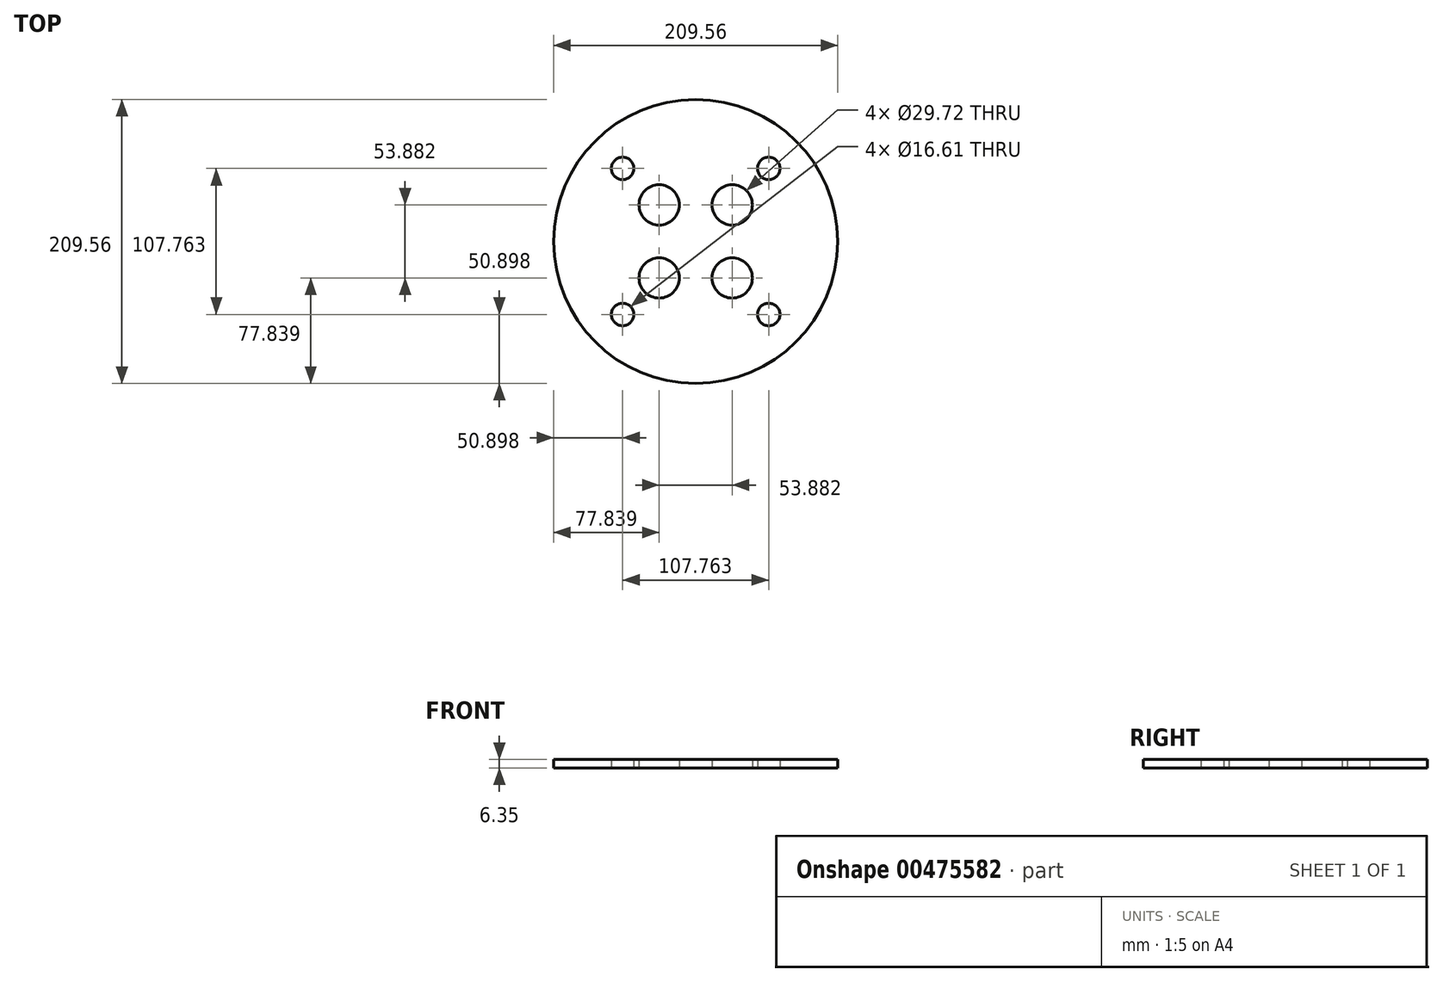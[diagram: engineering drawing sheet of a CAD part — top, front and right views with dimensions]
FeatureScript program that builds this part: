
annotation { "Feature Type Name" : "Feature", "Feature Type Description" : "" }
export const myFeature = defineFeature(function(context is Context, id is Id, definition is map)
    precondition{}
    {
        {
            var Q0;
            Q0=qCreatedBy(makeId("Top.planeOp"),FACE);
            var sketch = newSketch(context, id + "F0", { "sketchPlane" : qUnion([Q0])});
            skCircle(sketch, "E0", {"center": v(0, 0) * mm, "radius": 104.78 * mm});
            skLineSegment(sketch, "E1", {"start": v(0, 0) * mm, "end": v(53.88, 53.88) * mm});
            skLineSegment(sketch, "E2", {"start": v(0, 0) * mm, "end": v(53.88, -53.88) * mm});
            skLineSegment(sketch, "E3", {"start": v(0, 0) * mm, "end": v(-53.88, -53.88) * mm});
            skPoint(sketch, "E4", {"position": v(-26.94, 26.94) * mm});
            skPoint(sketch, "E5", {"position": v(26.94, 26.94) * mm});
            skPoint(sketch, "E6", {"position": v(26.94, -26.94) * mm});
            skPoint(sketch, "E7", {"position": v(-26.94, -26.94) * mm});
            skLineSegment(sketch, "E8", {"start": v(0, 0) * mm, "end": v(-53.88, 53.88) * mm});
            skPoint(sketch, "E9", {"position": v(-53.88, 53.88) * mm});
            skPoint(sketch, "E10", {"position": v(-53.88, -53.88) * mm});
            skPoint(sketch, "E11", {"position": v(53.88, 53.88) * mm});
            skPoint(sketch, "E12", {"position": v(53.88, -53.88) * mm});
            skSolve(sketch);
        }
        {
            var Q0;
            Q0=makeQuery(id+"F0.imprint","IMPRINT",FACE,{"disambiguationData":[TD([[makeQuery(id+"F0.imprint","IMPRINT",EDGE,{"derivedFrom":sQuery(id+"F0.wireOp",EDGE,"E0")}),1.0]])]});
            extrude(context, id + "F1", {"entities" : qUnion([Q0]), "depth" : 6.35 * mm});
        }
        {
            var Q0;
            Q0=sQuery(id+"F0.wireOp",VERTEX,"E4");
            var Q1;
            Q1=makeQuery(id+"F1.opExtrude","SWEPT_BODY",BODY,{"disambiguationData":[OSD([sQuery(id+"F0.wireOp",EDGE,"E0")])]});
            hole(context, id + "F2", {"style" : HoleStyle.SIMPLE, "endStyle" : HoleEndStyle.THROUGH, "oppositeDirection" : true, "holeDiameter" : 29.72 * mm, "isTappedThrough" : true, "tappedDepth" : 12.7 * mm, "tapClearance" : 3, "locations" : qUnion([Q0]), "scope" : qUnion([Q1])});
        }
        {
            var Q0;
            Q0=sQuery(id+"F0.wireOp",VERTEX,"E5");
            var Q1;
            Q1=makeQuery(id+"F1.opExtrude","SWEPT_BODY",BODY,{"disambiguationData":[OSD([sQuery(id+"F0.wireOp",EDGE,"E0")])]});
            hole(context, id + "F3", {"style" : HoleStyle.SIMPLE, "endStyle" : HoleEndStyle.THROUGH, "oppositeDirection" : true, "holeDiameter" : 29.72 * mm, "isTappedThrough" : true, "tappedDepth" : 12.7 * mm, "tapClearance" : 3, "locations" : qUnion([Q0]), "scope" : qUnion([Q1])});
        }
        {
            var Q0;
            Q0=sQuery(id+"F0.wireOp",VERTEX,"E7");
            var Q1;
            Q1=makeQuery(id+"F1.opExtrude","SWEPT_BODY",BODY,{"disambiguationData":[OSD([sQuery(id+"F0.wireOp",EDGE,"E0")])]});
            hole(context, id + "F4", {"style" : HoleStyle.SIMPLE, "endStyle" : HoleEndStyle.THROUGH, "oppositeDirection" : true, "holeDiameter" : 29.72 * mm, "isTappedThrough" : true, "tappedDepth" : 12.7 * mm, "tapClearance" : 3, "locations" : qUnion([Q0]), "scope" : qUnion([Q1])});
        }
        {
            var Q0;
            Q0=sQuery(id+"F0.wireOp",VERTEX,"E6");
            var Q1;
            Q1=makeQuery(id+"F1.opExtrude","SWEPT_BODY",BODY,{"disambiguationData":[OSD([sQuery(id+"F0.wireOp",EDGE,"E0")])]});
            hole(context, id + "F5", {"style" : HoleStyle.SIMPLE, "endStyle" : HoleEndStyle.THROUGH, "oppositeDirection" : true, "holeDiameter" : 29.72 * mm, "isTappedThrough" : true, "tappedDepth" : 12.7 * mm, "tapClearance" : 3, "locations" : qUnion([Q0]), "scope" : qUnion([Q1])});
        }
        {
            var Q0;
            Q0=sQuery(id+"F0.wireOp",VERTEX,"E9");
            var Q1;
            Q1=makeQuery(id+"F1.opExtrude","SWEPT_BODY",BODY,{"disambiguationData":[OSD([sQuery(id+"F0.wireOp",EDGE,"E0")])]});
            hole(context, id + "F6", {"style" : HoleStyle.SIMPLE, "endStyle" : HoleEndStyle.THROUGH, "oppositeDirection" : true, "holeDiameter" : 16.6 * mm, "isTappedThrough" : true, "tappedDepth" : 12.7 * mm, "tapClearance" : 3, "locations" : qUnion([Q0]), "scope" : qUnion([Q1])});
        }
        {
            var Q0;
            Q0=sQuery(id+"F0.wireOp",VERTEX,"E11");
            var Q1;
            Q1=makeQuery(id+"F1.opExtrude","SWEPT_BODY",BODY,{"disambiguationData":[OSD([sQuery(id+"F0.wireOp",EDGE,"E0")])]});
            hole(context, id + "F7", {"style" : HoleStyle.SIMPLE, "endStyle" : HoleEndStyle.THROUGH, "oppositeDirection" : true, "holeDiameter" : 16.6 * mm, "isTappedThrough" : true, "tappedDepth" : 12.7 * mm, "tapClearance" : 3, "locations" : qUnion([Q0]), "scope" : qUnion([Q1])});
        }
        {
            var Q0;
            Q0=sQuery(id+"F0.wireOp",VERTEX,"E10");
            var Q1;
            Q1=makeQuery(id+"F1.opExtrude","SWEPT_BODY",BODY,{"disambiguationData":[OSD([sQuery(id+"F0.wireOp",EDGE,"E0")])]});
            hole(context, id + "F8", {"style" : HoleStyle.SIMPLE, "endStyle" : HoleEndStyle.THROUGH, "oppositeDirection" : true, "holeDiameter" : 16.6 * mm, "isTappedThrough" : true, "tappedDepth" : 12.7 * mm, "tapClearance" : 3, "locations" : qUnion([Q0]), "scope" : qUnion([Q1])});
        }
        {
            var Q0;
            Q0=sQuery(id+"F0.wireOp",VERTEX,"E12");
            var Q1;
            Q1=makeQuery(id+"F1.opExtrude","SWEPT_BODY",BODY,{"disambiguationData":[OSD([sQuery(id+"F0.wireOp",EDGE,"E0")])]});
            hole(context, id + "F9", {"style" : HoleStyle.SIMPLE, "endStyle" : HoleEndStyle.THROUGH, "oppositeDirection" : true, "holeDiameter" : 16.6 * mm, "isTappedThrough" : true, "tappedDepth" : 12.7 * mm, "tapClearance" : 3, "locations" : qUnion([Q0]), "scope" : qUnion([Q1])});
        }
    });
